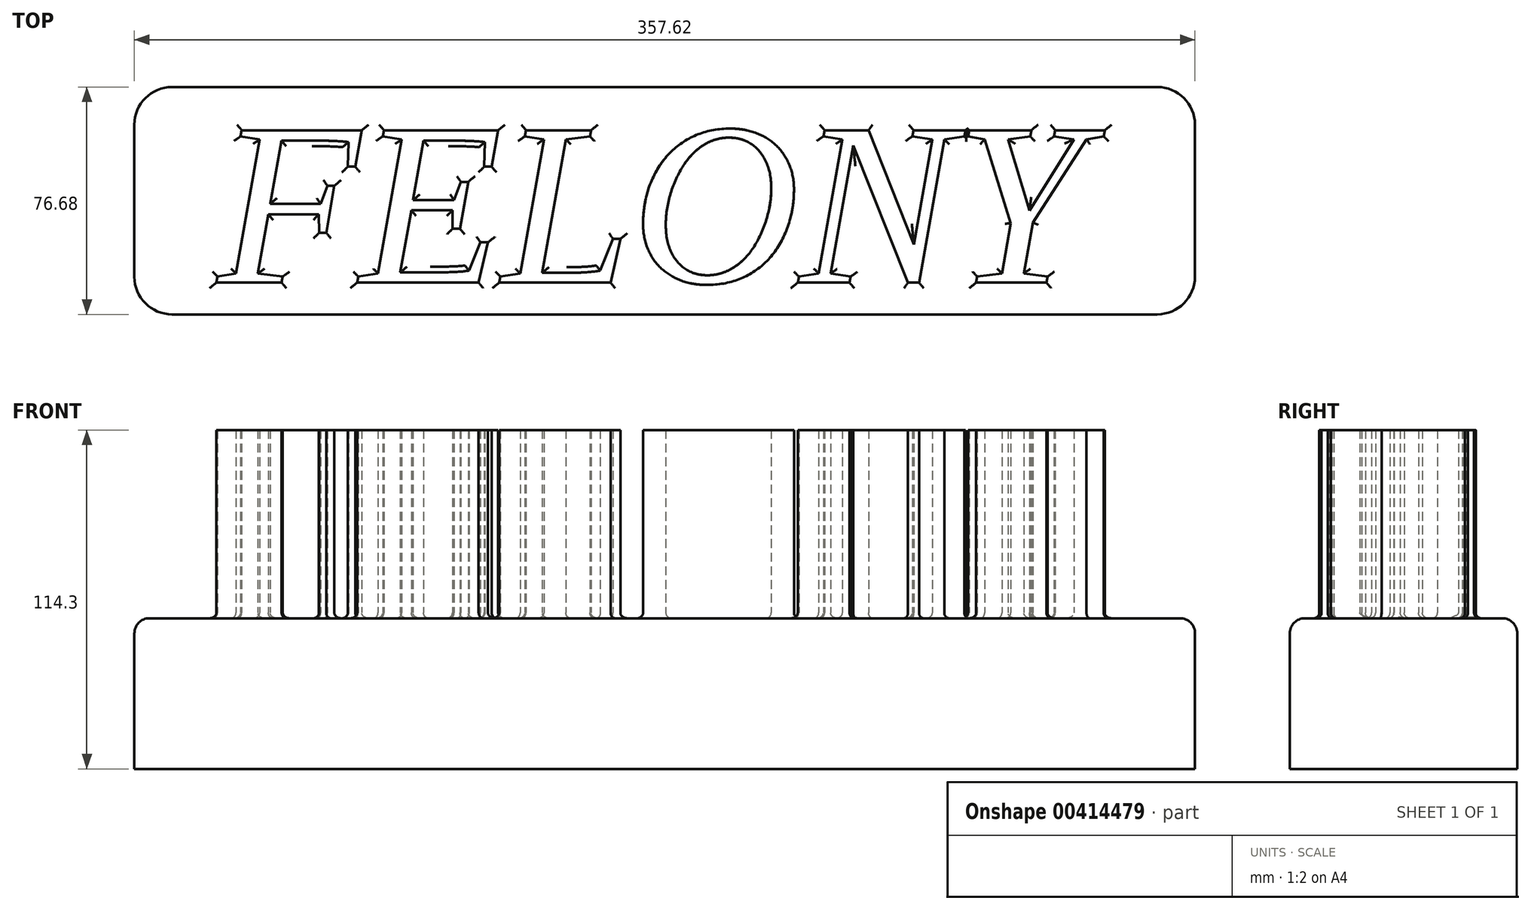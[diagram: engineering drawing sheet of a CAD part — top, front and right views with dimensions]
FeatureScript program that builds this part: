
annotation { "Feature Type Name" : "Feature", "Feature Type Description" : "" }
export const myFeature = defineFeature(function(context is Context, id is Id, definition is map)
    precondition{}
    {
        {
            var Q0;
            Q0=qCreatedBy(makeId("Top.planeOp"),FACE);
            var sketch = newSketch(context, id + "F0", { "sketchPlane" : qUnion([Q0])});
            skLineSegment(sketch, "E0.bottom", {"start": v(-166.11, -38.34) * mm, "end": v(166.11, -38.34) * mm});
            skLineSegment(sketch, "E0.top", {"start": v(-166.11, 38.34) * mm, "end": v(166.11, 38.34) * mm});
            skLineSegment(sketch, "E0.left", {"start": v(-178.81, -25.64) * mm, "end": v(-178.81, 25.64) * mm});
            skLineSegment(sketch, "E0.right", {"start": v(178.81, -25.64) * mm, "end": v(178.81, 25.64) * mm});
            skPoint(sketch, "E0.middle", {"position": v(0, 0) * mm});
            skPoint(sketch, "E1.visualSharp", {"position": v(-178.81, 38.34) * mm});
            skArc(sketch, "E1.filletArc", {"start": v(-166.11, 38.34) * mm, "mid": v(-175.1, 34.62) * mm, "end": v(-178.81, 25.64) * mm});
            skPoint(sketch, "E2.visualSharp", {"position": v(-178.81, -38.34) * mm});
            skArc(sketch, "E2.filletArc", {"start": v(-178.81, -25.64) * mm, "mid": v(-175.1, -34.62) * mm, "end": v(-166.11, -38.34) * mm});
            skPoint(sketch, "E3.visualSharp", {"position": v(178.81, 38.34) * mm});
            skArc(sketch, "E3.filletArc", {"start": v(178.81, 25.64) * mm, "mid": v(175.1, 34.62) * mm, "end": v(166.11, 38.34) * mm});
            skPoint(sketch, "E4.visualSharp", {"position": v(178.81, -38.34) * mm});
            skArc(sketch, "E4.filletArc", {"start": v(166.11, -38.34) * mm, "mid": v(175.1, -34.62) * mm, "end": v(178.81, -25.64) * mm});
            skArc(sketch, "E5.0", {"start": v(-166.11, 47.86) * mm, "mid": v(-181.83, 41.35) * mm, "end": v(-188.34, 25.64) * mm});
            skLineSegment(sketch, "E6.0", {"start": v(-166.11, 47.86) * mm, "end": v(166.11, 47.86) * mm});
            skArc(sketch, "E7.0", {"start": v(188.34, 25.64) * mm, "mid": v(181.83, 41.35) * mm, "end": v(166.11, 47.86) * mm});
            skLineSegment(sketch, "E8.0", {"start": v(188.34, -25.64) * mm, "end": v(188.34, 25.64) * mm});
            skLineSegment(sketch, "E8.1", {"start": v(-188.34, -25.64) * mm, "end": v(-188.34, 25.64) * mm});
            skArc(sketch, "E8.2", {"start": v(-188.34, -25.64) * mm, "mid": v(-181.83, -41.35) * mm, "end": v(-166.11, -47.86) * mm});
            skLineSegment(sketch, "E8.3", {"start": v(-166.11, -47.86) * mm, "end": v(166.11, -47.86) * mm});
            skArc(sketch, "E8.4", {"start": v(166.11, -47.86) * mm, "mid": v(181.83, -41.35) * mm, "end": v(188.34, -25.64) * mm});
            skCircle(sketch, "E9", {"center": v(-151.43, 43.52) * mm, "radius": 3.56 * mm});
            skCircle(sketch, "E10", {"center": v(-148.58, -43.42) * mm, "radius": 3.56 * mm});
            skCircle(sketch, "E11.MirrorC", {"center": v(151.43, 43.52) * mm, "radius": 3.56 * mm});
            skCircle(sketch, "E12.MirrorC", {"center": v(148.58, -43.42) * mm, "radius": 3.56 * mm});
            skLineSegment(sketch, "E13.0", {"start": v(-166.11, 35.19) * mm, "end": v(166.11, 35.19) * mm});
            skLineSegment(sketch, "E14.0", {"start": v(-166.11, -35.16) * mm, "end": v(166.11, -35.16) * mm});
            skLineSegment(sketch, "E15.0", {"start": v(-175.64, -25.64) * mm, "end": v(-175.64, 25.64) * mm});
            skLineSegment(sketch, "E16.0", {"start": v(175.64, -25.64) * mm, "end": v(175.64, 25.64) * mm});
            skArc(sketch, "E17.0", {"start": v(-166.11, 35.16) * mm, "mid": v(-172.85, 32.37) * mm, "end": v(-175.64, 25.64) * mm});
            skArc(sketch, "E18.0", {"start": v(-175.64, -25.64) * mm, "mid": v(-172.85, -32.37) * mm, "end": v(-166.11, -35.16) * mm});
            skArc(sketch, "E19.0", {"start": v(166.11, -35.16) * mm, "mid": v(172.85, -32.37) * mm, "end": v(175.64, -25.64) * mm});
            skArc(sketch, "E20.0", {"start": v(175.64, 25.64) * mm, "mid": v(172.85, 32.37) * mm, "end": v(166.11, 35.16) * mm});
            skSolve(sketch);
        }
        {
            var Q0;
            Q0 = qSketchRegion(id + "F0", true);
            var Q1;
            Q1=sQuery(id+"F0.wireOp",EDGE,"E14.0");
            var Q2;
            Q2=sQuery(id+"F0.wireOp",EDGE,"E19.0");
            var Q3;
            Q3=sQuery(id+"F0.wireOp",EDGE,"E16.0");
            var Q4;
            Q4=sQuery(id+"F0.wireOp",EDGE,"E20.0");
            var Q5;
            Q5=sQuery(id+"F0.wireOp",EDGE,"E13.0");
            var Q6;
            Q6=sQuery(id+"F0.wireOp",EDGE,"E17.0");
            var Q7;
            Q7=sQuery(id+"F0.wireOp",EDGE,"E15.0");
            var Q8;
            Q8=sQuery(id+"F0.wireOp",EDGE,"E18.0");
            extrude(context, id + "F1", {"entities" : qUnion([Q0]), "bodyType" : ToolBodyType.SURFACE, "surfaceEntities" : qUnion([Q1, Q2, Q3, Q4, Q5, Q6, Q7, Q8]), "depth" : 50.8 * mm, "offsetDistance" : 25.4 * mm});
        }
        {
            var Q0;
            Q0=makeQuery(id+"F0.imprint","IMPRINT",FACE,{"disambiguationData":[TD([[makeQuery(id+"F0.imprint","IMPRINT",EDGE,{"derivedFrom":sQuery(id+"F0.wireOp",EDGE,"E0.bottom")}),1.0]])]});
            extrude(context, id + "F2", {"entities" : qUnion([Q0]), "depth" : 50.8 * mm, "offsetDistance" : 25.4 * mm});
        }
        {
            var Q0;
            Q0=makeQuery(id+"F2.opExtrude","CAP_FACE",FACE,{"disambiguationData":[OSD([sQuery(id+"F0.wireOp",EDGE,"E0.bottom"),sQuery(id+"F0.wireOp",EDGE,"E0.top"),sQuery(id+"F0.wireOp",EDGE,"E0.left"),sQuery(id+"F0.wireOp",EDGE,"E0.right"),sQuery(id+"F0.wireOp",EDGE,"E1.filletArc"),sQuery(id+"F0.wireOp",EDGE,"E2.filletArc"),sQuery(id+"F0.wireOp",EDGE,"E3.filletArc"),sQuery(id+"F0.wireOp",EDGE,"E4.filletArc")])],"isStart":false});
            var sketch = newSketch(context, id + "F3", { "sketchPlane" : qUnion([Q0])});
            skText(sketch, "E21", { "text": "FELONY ", "fontName": "Tinos-Italic.ttf"});
            const initialGuessF3  = {"E21": [-0.15074, -0.02764, 1, 0, 0.0565]};
            skSetInitialGuess(sketch, initialGuessF3);
            skSolve(sketch);
        }
        {
            var Q0;
            Q0 = qSketchRegion(id + "F3", true);
            extrude(context, id + "F4", {"entities" : qUnion([Q0]), "operationType" : NewBodyOperationType.ADD, "depth" : 5.08 * mm, "offsetDistance" : 25.4 * mm});
        }
        {
            var Q0;
            Q0=makeQuery(id+"F2.opExtrude","CAP_EDGE",EDGE,{"disambiguationData":[OSD([sQuery(id+"F0.wireOp",EDGE,"E0.bottom")])],"isStart":false});
            fillet(context, id + "F5", {"entities" : qUnion([Q0]), "radius" : 5.08 * mm, "tangentPropagation" : true, "allowEdgeOverflow" : false});
        }
        {
            var Q0;
            Q0=makeQuery(id+"F4.opExtrude","CAP_EDGE",EDGE,{"disambiguationData":[OSD([sQuery(id+"F3.wireOp",EDGE,"E21.sketch_text.stroke-125")])],"isStart":true});
            var Q1;
            Q1=makeQuery(id+"F4.opExtrude","CAP_EDGE",EDGE,{"disambiguationData":[OSD([sQuery(id+"F3.wireOp",EDGE,"E21.sketch_text.stroke-124")])],"isStart":true});
            var Q2;
            Q2=makeQuery(id+"F4.opExtrude","CAP_EDGE",EDGE,{"disambiguationData":[OSD([sQuery(id+"F3.wireOp",EDGE,"E21.sketch_text.stroke-126")])],"isStart":true});
            var Q3;
            Q3=makeQuery(id+"F4.opExtrude","CAP_EDGE",EDGE,{"disambiguationData":[OSD([sQuery(id+"F3.wireOp",EDGE,"E21.sketch_text.stroke-123")])],"isStart":true});
            var Q4;
            Q4=makeQuery(id+"F4.opExtrude","CAP_EDGE",EDGE,{"disambiguationData":[OSD([sQuery(id+"F3.wireOp",EDGE,"E21.sketch_text.stroke-107")])],"isStart":true});
            var Q5;
            Q5=makeQuery(id+"F4.opExtrude","CAP_EDGE",EDGE,{"disambiguationData":[OSD([sQuery(id+"F3.wireOp",EDGE,"E21.sketch_text.stroke-108")])],"isStart":true});
            var Q6;
            {var subQ0=sQuery(id+"F0.wireOp",EDGE,"E0.top");var subQ1=sQuery(id+"F0.wireOp",EDGE,"E0.right");var subQ2=sQuery(id+"F0.wireOp",EDGE,"E0.bottom");var subQ3=sQuery(id+"F0.wireOp",EDGE,"E1.filletArc");var subQ4=sQuery(id+"F0.wireOp",EDGE,"E2.filletArc");var subQ5=sQuery(id+"F0.wireOp",EDGE,"E3.filletArc");var subQ6=sQuery(id+"F0.wireOp",EDGE,"E4.filletArc");var subQ7=sQuery(id+"F0.wireOp",EDGE,"E0.left");Q6=makeQuery(id+"F4.boolean.opBoolean","SPLIT",FACE,{"disambiguationData":[TD([makeQuery(id+"F2.opExtrude","SWEPT_FACE",FACE,{"disambiguationData":[OSD([subQ2])]})])],"derivedFrom":makeQuery(id+"F2.opExtrude","CAP_FACE",FACE,{"disambiguationData":[OSD([subQ2,subQ0,subQ7,subQ1,subQ3,subQ4,subQ5,subQ6])],"isStart":false})});}
            var Q7;
            Q7=makeQuery(id+"F4.boolean.opBoolean","SPLIT",FACE,{"disambiguationData":[TD([makeQuery(id+"F4.opExtrude","SWEPT_FACE",FACE,{"disambiguationData":[OSD([sQuery(id+"F3.wireOp",EDGE,"E21.sketch_text.stroke-64")])]})])],"derivedFrom":makeQuery(id+"F2.opExtrude","CAP_FACE",FACE,{"disambiguationData":[OSD([sQuery(id+"F0.wireOp",EDGE,"E0.bottom"),sQuery(id+"F0.wireOp",EDGE,"E0.top"),sQuery(id+"F0.wireOp",EDGE,"E0.left"),sQuery(id+"F0.wireOp",EDGE,"E0.right"),sQuery(id+"F0.wireOp",EDGE,"E1.filletArc"),sQuery(id+"F0.wireOp",EDGE,"E2.filletArc"),sQuery(id+"F0.wireOp",EDGE,"E3.filletArc"),sQuery(id+"F0.wireOp",EDGE,"E4.filletArc")])],"isStart":false})});
            fillet(context, id + "F6", {"entities" : qUnion([Q0, Q1, Q2, Q3, Q4, Q5, Q6, Q7]), "radius" : 1.9 * mm, "tangentPropagation" : true, "allowEdgeOverflow" : false});
        }
        {
            var Q0;
            Q0=makeQuery(id+"F4.opExtrude","CAP_EDGE",EDGE,{"disambiguationData":[OSD([sQuery(id+"F3.wireOp",EDGE,"E21.sketch_text.stroke-77")])],"isStart":false});
            var Q1;
            Q1=makeQuery(id+"F4.opExtrude","CAP_EDGE",EDGE,{"disambiguationData":[OSD([sQuery(id+"F3.wireOp",EDGE,"E21.sketch_text.stroke-68")])],"isStart":false});
            var Q2;
            Q2=makeQuery(id+"F4.opExtrude","CAP_EDGE",EDGE,{"disambiguationData":[OSD([sQuery(id+"F3.wireOp",EDGE,"E21.sketch_text.stroke-94")])],"isStart":false});
            var Q3;
            Q3=makeQuery(id+"F4.opExtrude","CAP_EDGE",EDGE,{"disambiguationData":[OSD([sQuery(id+"F3.wireOp",EDGE,"E21.sketch_text.stroke-93")])],"isStart":false});
            var Q4;
            Q4=makeQuery(id+"F4.opExtrude","CAP_EDGE",EDGE,{"disambiguationData":[OSD([sQuery(id+"F3.wireOp",EDGE,"E21.sketch_text.stroke-92")])],"isStart":false});
            var Q5;
            Q5=makeQuery(id+"F4.opExtrude","CAP_EDGE",EDGE,{"disambiguationData":[OSD([sQuery(id+"F3.wireOp",EDGE,"E21.sketch_text.stroke-91")])],"isStart":false});
            var Q6;
            Q6=makeQuery(id+"F4.opExtrude","CAP_FACE",FACE,{"disambiguationData":[OSD([sQuery(id+"F3.wireOp",EDGE,"E21.sketch_text.stroke-86"),sQuery(id+"F3.wireOp",EDGE,"E21.sketch_text.stroke-87"),sQuery(id+"F3.wireOp",EDGE,"E21.sketch_text.stroke-88"),sQuery(id+"F3.wireOp",EDGE,"E21.sketch_text.stroke-89"),sQuery(id+"F3.wireOp",EDGE,"E21.sketch_text.stroke-90"),sQuery(id+"F3.wireOp",EDGE,"E21.sketch_text.stroke-91"),sQuery(id+"F3.wireOp",EDGE,"E21.sketch_text.stroke-92"),sQuery(id+"F3.wireOp",EDGE,"E21.sketch_text.stroke-93"),sQuery(id+"F3.wireOp",EDGE,"E21.sketch_text.stroke-94"),sQuery(id+"F3.wireOp",EDGE,"E21.sketch_text.stroke-95"),sQuery(id+"F3.wireOp",EDGE,"E21.sketch_text.stroke-96"),sQuery(id+"F3.wireOp",EDGE,"E21.sketch_text.stroke-97"),sQuery(id+"F3.wireOp",EDGE,"E21.sketch_text.stroke-98"),sQuery(id+"F3.wireOp",EDGE,"E21.sketch_text.stroke-99"),sQuery(id+"F3.wireOp",EDGE,"E21.sketch_text.stroke-100"),sQuery(id+"F3.wireOp",EDGE,"E21.sketch_text.stroke-101"),sQuery(id+"F3.wireOp",EDGE,"E21.sketch_text.stroke-102"),sQuery(id+"F3.wireOp",EDGE,"E21.sketch_text.stroke-103"),sQuery(id+"F3.wireOp",EDGE,"E21.sketch_text.stroke-104"),sQuery(id+"F3.wireOp",EDGE,"E21.sketch_text.stroke-105")])],"isStart":false});
            var Q7;
            Q7=makeQuery(id+"F4.opExtrude","CAP_EDGE",EDGE,{"disambiguationData":[OSD([sQuery(id+"F3.wireOp",EDGE,"E21.sketch_text.stroke-111")])],"isStart":false});
            var Q8;
            Q8=makeQuery(id+"F4.opExtrude","CAP_FACE",FACE,{"disambiguationData":[OSD([sQuery(id+"F3.wireOp",EDGE,"E21.sketch_text.stroke-106"),sQuery(id+"F3.wireOp",EDGE,"E21.sketch_text.stroke-107"),sQuery(id+"F3.wireOp",EDGE,"E21.sketch_text.stroke-108"),sQuery(id+"F3.wireOp",EDGE,"E21.sketch_text.stroke-109"),sQuery(id+"F3.wireOp",EDGE,"E21.sketch_text.stroke-110"),sQuery(id+"F3.wireOp",EDGE,"E21.sketch_text.stroke-111"),sQuery(id+"F3.wireOp",EDGE,"E21.sketch_text.stroke-112"),sQuery(id+"F3.wireOp",EDGE,"E21.sketch_text.stroke-113"),sQuery(id+"F3.wireOp",EDGE,"E21.sketch_text.stroke-114"),sQuery(id+"F3.wireOp",EDGE,"E21.sketch_text.stroke-115"),sQuery(id+"F3.wireOp",EDGE,"E21.sketch_text.stroke-116"),sQuery(id+"F3.wireOp",EDGE,"E21.sketch_text.stroke-117"),sQuery(id+"F3.wireOp",EDGE,"E21.sketch_text.stroke-118"),sQuery(id+"F3.wireOp",EDGE,"E21.sketch_text.stroke-119"),sQuery(id+"F3.wireOp",EDGE,"E21.sketch_text.stroke-120"),sQuery(id+"F3.wireOp",EDGE,"E21.sketch_text.stroke-121"),sQuery(id+"F3.wireOp",EDGE,"E21.sketch_text.stroke-122"),sQuery(id+"F3.wireOp",EDGE,"E21.sketch_text.stroke-123"),sQuery(id+"F3.wireOp",EDGE,"E21.sketch_text.stroke-124"),sQuery(id+"F3.wireOp",EDGE,"E21.sketch_text.stroke-125"),sQuery(id+"F3.wireOp",EDGE,"E21.sketch_text.stroke-126")])],"isStart":false});
            var Q9;
            Q9=makeQuery(id+"F4.opExtrude","CAP_EDGE",EDGE,{"disambiguationData":[OSD([sQuery(id+"F3.wireOp",EDGE,"E21.sketch_text.stroke-110")])],"isStart":false});
            var Q10;
            Q10=makeQuery(id+"F4.opExtrude","CAP_EDGE",EDGE,{"disambiguationData":[OSD([sQuery(id+"F3.wireOp",EDGE,"E21.sketch_text.stroke-57")])],"isStart":false});
            var Q11;
            Q11=makeQuery(id+"F4.opExtrude","CAP_EDGE",EDGE,{"disambiguationData":[OSD([sQuery(id+"F3.wireOp",EDGE,"E21.sketch_text.stroke-41")])],"isStart":false});
            var Q12;
            Q12=makeQuery(id+"F4.opExtrude","CAP_EDGE",EDGE,{"disambiguationData":[OSD([sQuery(id+"F3.wireOp",EDGE,"E21.sketch_text.stroke-38")])],"isStart":false});
            var Q13;
            Q13=makeQuery(id+"F4.opExtrude","CAP_EDGE",EDGE,{"disambiguationData":[OSD([sQuery(id+"F3.wireOp",EDGE,"E21.sketch_text.stroke-37")])],"isStart":false});
            var Q14;
            Q14=makeQuery(id+"F4.opExtrude","CAP_EDGE",EDGE,{"disambiguationData":[OSD([sQuery(id+"F3.wireOp",EDGE,"E21.sketch_text.stroke-35")])],"isStart":false});
            var Q15;
            Q15=makeQuery(id+"F4.opExtrude","CAP_EDGE",EDGE,{"disambiguationData":[OSD([sQuery(id+"F3.wireOp",EDGE,"E21.sketch_text.stroke-36")])],"isStart":false});
            var Q16;
            Q16=makeQuery(id+"F4.opExtrude","CAP_EDGE",EDGE,{"disambiguationData":[OSD([sQuery(id+"F3.wireOp",EDGE,"E21.sketch_text.stroke-34")])],"isStart":false});
            var Q17;
            Q17=makeQuery(id+"F4.opExtrude","CAP_EDGE",EDGE,{"disambiguationData":[OSD([sQuery(id+"F3.wireOp",EDGE,"E21.sketch_text.stroke-33")])],"isStart":false});
            var Q18;
            Q18=makeQuery(id+"F4.opExtrude","CAP_EDGE",EDGE,{"disambiguationData":[OSD([sQuery(id+"F3.wireOp",EDGE,"E21.sketch_text.stroke-32")])],"isStart":false});
            var Q19;
            Q19=makeQuery(id+"F4.opExtrude","CAP_EDGE",EDGE,{"disambiguationData":[OSD([sQuery(id+"F3.wireOp",EDGE,"E21.sketch_text.stroke-27")])],"isStart":false});
            var Q20;
            Q20=makeQuery(id+"F4.opExtrude","CAP_EDGE",EDGE,{"disambiguationData":[OSD([sQuery(id+"F3.wireOp",EDGE,"E21.sketch_text.stroke-26")])],"isStart":false});
            var Q21;
            Q21=makeQuery(id+"F4.opExtrude","CAP_EDGE",EDGE,{"disambiguationData":[OSD([sQuery(id+"F3.wireOp",EDGE,"E21.sketch_text.stroke-25")])],"isStart":false});
            var Q22;
            Q22=makeQuery(id+"F4.opExtrude","CAP_EDGE",EDGE,{"disambiguationData":[OSD([sQuery(id+"F3.wireOp",EDGE,"E21.sketch_text.stroke-29")])],"isStart":false});
            var Q23;
            Q23=makeQuery(id+"F4.opExtrude","CAP_EDGE",EDGE,{"disambiguationData":[OSD([sQuery(id+"F3.wireOp",EDGE,"E21.sketch_text.stroke-62")])],"isStart":false});
            var Q24;
            Q24=makeQuery(id+"F4.opExtrude","CAP_EDGE",EDGE,{"disambiguationData":[OSD([sQuery(id+"F3.wireOp",EDGE,"E21.sketch_text.stroke-63")])],"isStart":false});
            var Q25;
            Q25=makeQuery(id+"F4.opExtrude","CAP_EDGE",EDGE,{"disambiguationData":[OSD([sQuery(id+"F3.wireOp",EDGE,"E21.sketch_text.stroke-60")])],"isStart":false});
            var Q26;
            Q26=makeQuery(id+"F4.opExtrude","CAP_EDGE",EDGE,{"disambiguationData":[OSD([sQuery(id+"F3.wireOp",EDGE,"E21.sketch_text.stroke-59")])],"isStart":false});
            var Q27;
            Q27=makeQuery(id+"F4.opExtrude","CAP_EDGE",EDGE,{"disambiguationData":[OSD([sQuery(id+"F3.wireOp",EDGE,"E21.sketch_text.stroke-58")])],"isStart":false});
            var Q28;
            Q28=makeQuery(id+"F4.opExtrude","CAP_EDGE",EDGE,{"disambiguationData":[OSD([sQuery(id+"F3.wireOp",EDGE,"E21.sketch_text.stroke-55")])],"isStart":false});
            var Q29;
            Q29=makeQuery(id+"F4.opExtrude","CAP_EDGE",EDGE,{"disambiguationData":[OSD([sQuery(id+"F3.wireOp",EDGE,"E21.sketch_text.stroke-54")])],"isStart":false});
            var Q30;
            Q30=makeQuery(id+"F4.opExtrude","CAP_EDGE",EDGE,{"disambiguationData":[OSD([sQuery(id+"F3.wireOp",EDGE,"E21.sketch_text.stroke-50")])],"isStart":false});
            var Q31;
            Q31=makeQuery(id+"F4.opExtrude","CAP_EDGE",EDGE,{"disambiguationData":[OSD([sQuery(id+"F3.wireOp",EDGE,"E21.sketch_text.stroke-49")])],"isStart":false});
            var Q32;
            Q32=makeQuery(id+"F4.opExtrude","CAP_EDGE",EDGE,{"disambiguationData":[OSD([sQuery(id+"F3.wireOp",EDGE,"E21.sketch_text.stroke-53")])],"isStart":false});
            var Q33;
            Q33=makeQuery(id+"F4.opExtrude","CAP_EDGE",EDGE,{"disambiguationData":[OSD([sQuery(id+"F3.wireOp",EDGE,"E21.sketch_text.stroke-31")])],"isStart":false});
            var Q34;
            Q34=makeQuery(id+"F4.opExtrude","CAP_EDGE",EDGE,{"disambiguationData":[OSD([sQuery(id+"F3.wireOp",EDGE,"E21.sketch_text.stroke-39")])],"isStart":false});
            var Q35;
            Q35=makeQuery(id+"F4.opExtrude","CAP_EDGE",EDGE,{"disambiguationData":[OSD([sQuery(id+"F3.wireOp",EDGE,"E21.sketch_text.stroke-42")])],"isStart":false});
            var Q36;
            Q36=makeQuery(id+"F4.opExtrude","CAP_EDGE",EDGE,{"disambiguationData":[OSD([sQuery(id+"F3.wireOp",EDGE,"E21.sketch_text.stroke-43")])],"isStart":false});
            var Q37;
            Q37=makeQuery(id+"F4.opExtrude","CAP_EDGE",EDGE,{"disambiguationData":[OSD([sQuery(id+"F3.wireOp",EDGE,"E21.sketch_text.stroke-44")])],"isStart":false});
            var Q38;
            Q38=makeQuery(id+"F4.opExtrude","CAP_EDGE",EDGE,{"disambiguationData":[OSD([sQuery(id+"F3.wireOp",EDGE,"E21.sketch_text.stroke-45")])],"isStart":false});
            var Q39;
            Q39=makeQuery(id+"F4.opExtrude","CAP_EDGE",EDGE,{"disambiguationData":[OSD([sQuery(id+"F3.wireOp",EDGE,"E21.sketch_text.stroke-46")])],"isStart":false});
            var Q40;
            Q40=makeQuery(id+"F4.opExtrude","CAP_EDGE",EDGE,{"disambiguationData":[OSD([sQuery(id+"F3.wireOp",EDGE,"E21.sketch_text.stroke-48")])],"isStart":false});
            var Q41;
            Q41=makeQuery(id+"F4.opExtrude","CAP_FACE",FACE,{"disambiguationData":[OSD([sQuery(id+"F3.wireOp",EDGE,"E21.sketch_text.stroke-0"),sQuery(id+"F3.wireOp",EDGE,"E21.sketch_text.stroke-1"),sQuery(id+"F3.wireOp",EDGE,"E21.sketch_text.stroke-2"),sQuery(id+"F3.wireOp",EDGE,"E21.sketch_text.stroke-3"),sQuery(id+"F3.wireOp",EDGE,"E21.sketch_text.stroke-4"),sQuery(id+"F3.wireOp",EDGE,"E21.sketch_text.stroke-5"),sQuery(id+"F3.wireOp",EDGE,"E21.sketch_text.stroke-6"),sQuery(id+"F3.wireOp",EDGE,"E21.sketch_text.stroke-7"),sQuery(id+"F3.wireOp",EDGE,"E21.sketch_text.stroke-8"),sQuery(id+"F3.wireOp",EDGE,"E21.sketch_text.stroke-9"),sQuery(id+"F3.wireOp",EDGE,"E21.sketch_text.stroke-10"),sQuery(id+"F3.wireOp",EDGE,"E21.sketch_text.stroke-11"),sQuery(id+"F3.wireOp",EDGE,"E21.sketch_text.stroke-12"),sQuery(id+"F3.wireOp",EDGE,"E21.sketch_text.stroke-13"),sQuery(id+"F3.wireOp",EDGE,"E21.sketch_text.stroke-14"),sQuery(id+"F3.wireOp",EDGE,"E21.sketch_text.stroke-15"),sQuery(id+"F3.wireOp",EDGE,"E21.sketch_text.stroke-16"),sQuery(id+"F3.wireOp",EDGE,"E21.sketch_text.stroke-17"),sQuery(id+"F3.wireOp",EDGE,"E21.sketch_text.stroke-18"),sQuery(id+"F3.wireOp",EDGE,"E21.sketch_text.stroke-19"),sQuery(id+"F3.wireOp",EDGE,"E21.sketch_text.stroke-20"),sQuery(id+"F3.wireOp",EDGE,"E21.sketch_text.stroke-21"),sQuery(id+"F3.wireOp",EDGE,"E21.sketch_text.stroke-22")])],"isStart":false});
            fillet(context, id + "F7", {"entities" : qUnion([Q0, Q1, Q2, Q3, Q4, Q5, Q6, Q7, Q8, Q9, Q10, Q11, Q12, Q13, Q14, Q15, Q16, Q17, Q18, Q19, Q20, Q21, Q22, Q23, Q24, Q25, Q26, Q27, Q28, Q29, Q30, Q31, Q32, Q33, Q34, Q35, Q36, Q37, Q38, Q39, Q40, Q41]), "radius" : 1.27 * mm, "tangentPropagation" : true, "allowEdgeOverflow" : false});
        }
        {
            var Q0;
            Q0 = qConstructionFilter(qBodyType(qCreatedBy(id + "F0" ,EDGE), BodyType.WIRE), ConstructionObject.NO);
            extrude(context, id + "F8", {"bodyType" : ToolBodyType.SURFACE, "surfaceEntities" : qUnion([Q0]), "depth" : 25.4 * mm, "offsetDistance" : 25.4 * mm});
        }
        {
            var Q0;
            Q0 = qSketchRegion(id + "F3", true);
            extrude(context, id + "F9", {"entities" : qUnion([Q0]), "operationType" : NewBodyOperationType.ADD, "depth" : 63.5 * mm});
        }
    });
